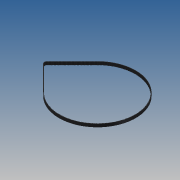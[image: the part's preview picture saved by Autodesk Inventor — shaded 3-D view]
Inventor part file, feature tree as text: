
AUTODESK INVENTOR PART (.ipt)
format: ipt  version: 2013 (Build 170138000, 138)  size: 738,816 bytes
history: native  units: mm
features: sketch x5, extrude x4, pattern_linear x1
ambient origin geometry x8: Origin, YZ Plane, XZ Plane, XY Plane, X Axis, Y Axis, Z Axis, Center Point
bodies: Solid1 (feature_tree)
feature tree (10):
  extrude  "Extrusion1"  Depth=74.802823mm
  extrude  "Extrusion2"  Depth=15.719465mm
  extrude  "Extrusion4"  Depth=0.375mm
  sketch  "Sketch8"  dims[d15=6.0mm d16=0.0mm d17=6.0mm d18=0.0mm d19=2500.0mm]
  extrude  "Extrusion5"  Depth=0.629mm
  pattern_linear  "Rectangular Pattern1"  Spacing1=6.0mm  [1 undecoded]
  sketch  "Sketch1"  dims[d0=5.092958mm d2=74.802823mm]
  sketch  "Sketch2"  dims[d3=69.790089mm d4=15.719465mm]
  sketch  "Sketch5"  dims[d5=6.0mm d6=0.0mm d7=0.375mm]
  sketch  "Sketch7"  dims[d8=6.0mm d9=0.0mm d14=0.629mm]
note: 1 required parameter value undecoded (feature->parameter linkage not recoverable at this tier; creation-order binding heuristic only, values carry confidence <= 0.55)
